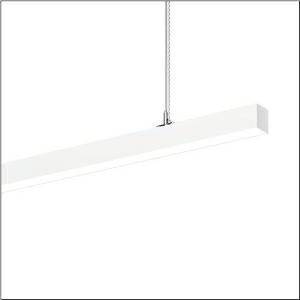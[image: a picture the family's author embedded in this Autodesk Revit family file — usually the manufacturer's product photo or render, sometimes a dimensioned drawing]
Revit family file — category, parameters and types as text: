
# Revit family: silica_21_51mx30tat4w
name_source: partatom
category: Lighting Fixtures
units: mm (PartAtom-declared; Revit-internal decimal feet)

## family parameters
Cut with Voids When Loaded = No
Host = Face
Light Source = No
Part Type = Normal
Room Calculation Point = No
Round Connector Dimension = Use Diameter
Shared = No

## types (1)
- --- (1 x LED, 4120 lm, 33.8 W, 6500K)
    Apparent Load = 34 VA
    CIE Flux Codes = 47 79 96 58 100
    Color Rendering = 80
    Color Temperature = 6500K
    Default Elevation = 1800 mm
    Description = Silica 21, office luminaire, primary optical cover: cover, of PMMA, opal, light emission: direct/indirect distribution, primary light characteristic: symmetric, installation type: suspended mounting, LED, rated luminous flux: 4.120lm, luminous efficacy: 116lm/W, light colour: 8tw, colour temperature: 2700..6500K, control gear: DALI DT8, with terminal, 3+2-pole, max. 2.5mm², mains connection: 220..240V, AC, 50/60Hz, rated input power: 35.5W, luminaire housing, of aluminium, traffic white (RAL 9016), length: 1.204mm, width: 53mm, height: 53mm, protection rating (complete): IP20, insulation class (complete): insulation class I (protective earthing), certification: CE, permissible operating ambient temperature: 0..+35°C, standard: EN 50419, packaging unit: 1 piece
    Height = 53 mm
    Lamp = 1 x LED
    Lamp Light Flux = 4120 lm
    Lamp Power = 33.8 W
    Lamp count = 1
    Length = 1204 mm
    Luminous efficacy = 122 lm/W
    Manufacturer = Siteco
    ModVariant = No
    Model = 51MX30TAT4W
    Mounting Place = Ceiling
    Mounting Type = Pendant
    Number of Poles = 1
    OnlyDefault = Yes
    Power Factor = 1
    Product Name = Silica 21
    Product group = office luminaire | ceiling pendant
    ProductGroupID = 903
    Protection Class = Protection class I
    Protection Degree = IP 20
    RLX_Detail_Level = 1
    RLX_Emergency_Light_Flux = 0 lm
    RLX_Emergency_Type = 0
    RLX_Emergency_Type_DB = No
    RlxData = <blob elided: 17637 chars, md5=479dad32>
    Socket = socket
    Standby Power = 0 W
    System Light Flux = 4120 lm
    System Power = 34 W
    Type Comments = individual setting
    Type Image = l_1349023.jpg
    URL = http://relux.com
    VarID = @adj_139151
    Voltage = 0 V
    Weight = 0.00 kg
    Width = 53 mm

## geometry (parser evidence)
native form markers: Blend x4, Sweep x14
no freeform markers — native parametric forms only
